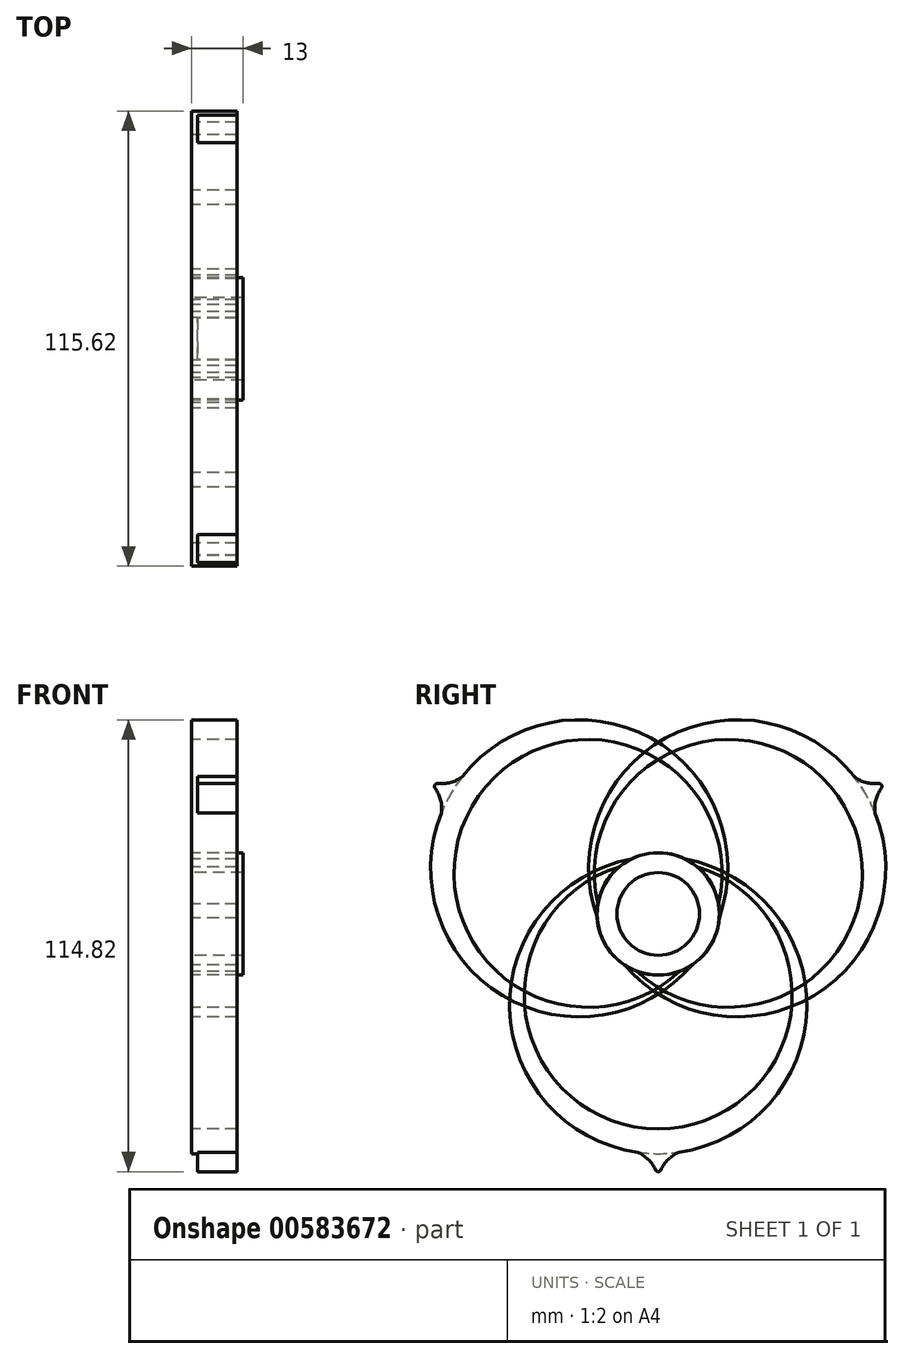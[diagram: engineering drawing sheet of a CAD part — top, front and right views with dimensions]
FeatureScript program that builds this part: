
annotation { "Feature Type Name" : "Feature", "Feature Type Description" : "" }
export const myFeature = defineFeature(function(context is Context, id is Id, definition is map)
    precondition{}
    {
        {
            var Q0;
            Q0=qCreatedBy(makeId("Right.planeOp"),FACE);
            var sketch = newSketch(context, id + "F0", { "sketchPlane" : qUnion([Q0])});
            skCircle(sketch, "E0", {"center": v(0, 0) * mm, "radius": 10.5 * mm});
            skCircle(sketch, "E1", {"center": v(0, 0) * mm, "radius": 15.53 * mm});
            skArc(sketch, "E2", {"start": v(-9.9, 11.96) * mm, "mid": v(0, -54.63) * mm, "end": v(9.9, 11.96) * mm});
            skArc(sketch, "E3", {"start": v(-6.86, 13.93) * mm, "mid": v(0, -60.92) * mm, "end": v(6.86, 13.93) * mm});
            skArc(sketch, "E4", {"start": v(0, -67.64) * mm, "mid": v(-1.68, -63.37) * mm, "end": v(-5.3, -60.54) * mm});
            skPoint(sketch, "E4.startSnap0", {"position": v(0, -60.92) * mm});
            skArc(sketch, "E5", {"start": v(5.3, -60.54) * mm, "mid": v(1.68, -63.37) * mm, "end": v(0, -67.64) * mm});
            skSolve(sketch);
        }
        {
            var Q0;
            Q0=makeQuery(id+"F0.imprint","IMPRINT",FACE,{"disambiguationData":[TD([[makeQuery(id+"F0.imprint","IMPRINT",EDGE,{"derivedFrom":sQuery(id+"F0.wireOp",EDGE,"E0")}),-1.0]])]});
            extrude(context, id + "F1", {"entities" : qUnion([Q0]), "depth" : 6.5 * mm, "offsetDistance" : 25.4 * mm, "hasSecondDirection" : true, "secondDirectionOppositeDirection" : true, "secondDirectionDepth" : 6.5 * mm});
        }
        {
            var Q0;
            {var subQ0=sQuery(id+"F0.wireOp",EDGE,"E2");Q0=makeQuery(id+"F0.imprint","IMPRINT",FACE,{"disambiguationData":[TD([[makeQuery(id+"F0.imprint","IMPRINT",EDGE,{"derivedFrom":subQ0}),-1.0]])]});}
            extrude(context, id + "F2", {"entities" : qUnion([Q0]), "operationType" : NewBodyOperationType.ADD, "depth" : 5 * mm, "offsetDistance" : 25.4 * mm, "hasSecondDirection" : true, "secondDirectionOppositeDirection" : true, "secondDirectionDepth" : 6.5 * mm});
        }
        {
            var Q0;
            {var subQ0=sQuery(id+"F0.wireOp",EDGE,"E4");Q0=makeQuery(id+"F0.imprint","IMPRINT",FACE,{"disambiguationData":[TD([[makeQuery(id+"F0.imprint","IMPRINT",EDGE,{"derivedFrom":subQ0}),-1.0]])]});}
            extrude(context, id + "F3", {"entities" : qUnion([Q0]), "operationType" : NewBodyOperationType.ADD, "depth" : 5 * mm, "offsetDistance" : 25.4 * mm, "hasSecondDirection" : true, "secondDirectionOppositeDirection" : true, "secondDirectionDepth" : 5 * mm});
        }
        {
            var Q0;
            Q0=makeQuery(id+"F1.opExtrude","SWEPT_BODY",BODY,{"disambiguationData":[OSD([sQuery(id+"F0.wireOp",EDGE,"E0"),sQuery(id+"F0.wireOp",EDGE,"E1")])]});
            var Q1;
            Q1=makeQuery(id+"F1.opExtrude","CAP_EDGE",EDGE,{"disambiguationData":[OSD([sQuery(id+"F0.wireOp",EDGE,"E0")])],"isStart":false});
            circularPattern(context, id + "F4", {"entities" : qUnion([Q0]), "axis" : qUnion([Q1]), "angle" : 360 * degree, "instanceCount" : 3, "equalSpace" : true});
        }
        {
            var Q0;
            Q0=makeQuery(id+"F4.opPattern","COPY",EDGE,{"derivedFrom":makeQuery(id+"F3.opExtrude","SWEPT_EDGE",EDGE,{"disambiguationData":[OSD([sQuery(id+"F0.wireOp",EDGE,"E4"),sQuery(id+"F0.wireOp",EDGE,"E5")])]}),"instanceName":"1"});
            var Q1;
            Q1=makeQuery(id+"F4.opPattern","COPY",EDGE,{"derivedFrom":makeQuery(id+"F3.opExtrude","SWEPT_EDGE",EDGE,{"disambiguationData":[OSD([sQuery(id+"F0.wireOp",EDGE,"E4"),sQuery(id+"F0.wireOp",EDGE,"E5")])]}),"instanceName":"2"});
            var Q2;
            Q2=makeQuery(id+"F3.opExtrude","SWEPT_EDGE",EDGE,{"disambiguationData":[OSD([sQuery(id+"F0.wireOp",EDGE,"E4"),sQuery(id+"F0.wireOp",EDGE,"E5")])]});
            fillet(context, id + "F5", {"entities" : qUnion([Q0, Q1, Q2]), "radius" : 0.76 * mm, "tangentPropagation" : true, "allowEdgeOverflow" : false});
        }
    });
